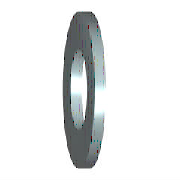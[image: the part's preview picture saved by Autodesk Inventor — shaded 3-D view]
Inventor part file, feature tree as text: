
AUTODESK INVENTOR PART (.ipt)
format: ipt  version: 2022.1 (Build 261234000, 234)  size: 107,520 bytes
history: native  units: mm (DEFAULTED — no unit token found)
features: extrude x1, other x1, plane x1, sketch x1
ambient origin geometry x7: Origin, YZ Plane, XY Plane, X Axis, Y Axis, Z Axis, Center Point
bodies: Solid1 (feature_tree)
feature tree (4):
  extrude  "Cuerpo"  Depth=0.5mm
  other  "Work Axis1"
  plane  "Work Plane1"
  sketch  "Boceto"  dims[d0=3.2mm d1=7.0mm d2=0.5mm d3=0.0mm d4=0.0mm d5=0.0mm d6=0.0mm d7=0.0mm]
